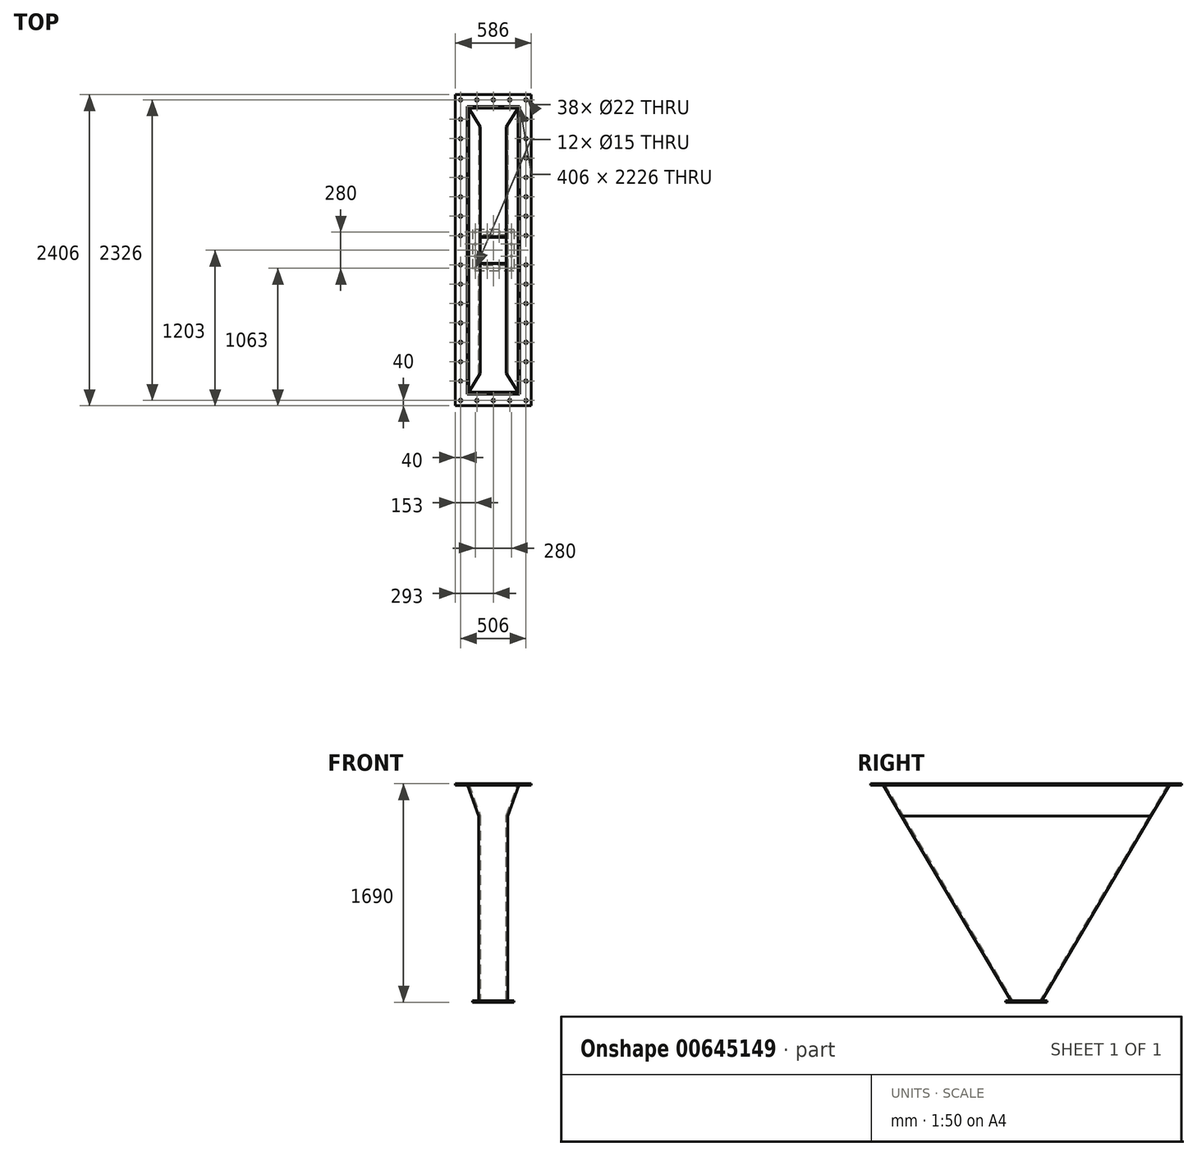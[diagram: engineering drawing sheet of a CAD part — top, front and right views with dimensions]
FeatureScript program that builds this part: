
annotation { "Feature Type Name" : "Feature", "Feature Type Description" : "" }
export const myFeature = defineFeature(function(context is Context, id is Id, definition is map)
    precondition{}
    {
        {
            var Q0;
            Q0=qCreatedBy(makeId("Front.planeOp"),FACE);
            var sketch = newSketch(context, id + "F0", { "sketchPlane" : qUnion([Q0])});
            skLineSegment(sketch, "E0", {"start": v(-203, 137.7) * mm, "end": v(203, 137.7) * mm});
            skLineSegment(sketch, "E1", {"start": v(0, 137.7) * mm, "end": v(0, -112.31) * mm, "construction": true});
            skLineSegment(sketch, "E2", {"start": v(-112, -112.31) * mm, "end": v(112, -112.31) * mm});
            skLineSegment(sketch, "E3", {"start": v(-203, 137.7) * mm, "end": v(-112, -112.31) * mm});
            skLineSegment(sketch, "E4", {"start": v(112, -112.31) * mm, "end": v(203, 137.7) * mm});
            skLineSegment(sketch, "E5", {"start": v(-112, -112.31) * mm, "end": v(-112, -1552.3) * mm});
            skLineSegment(sketch, "E6", {"start": v(-112, -1552.3) * mm, "end": v(112, -1552.3) * mm});
            skLineSegment(sketch, "E7", {"start": v(112, -1552.3) * mm, "end": v(112, -112.31) * mm});
            skLineSegment(sketch, "E8", {"start": v(-112, -112.31) * mm, "end": v(-112, 137.7) * mm, "construction": true});
            skLineSegment(sketch, "E9", {"start": v(112, -112.31) * mm, "end": v(112, 137.7) * mm, "construction": true});
            skSolve(sketch);
        }
        {
            var Q0;
            Q0=makeQuery(id+"F0.imprint","IMPRINT",FACE,{"disambiguationData":[TD([[makeQuery(id+"F0.imprint","IMPRINT",EDGE,{"derivedFrom":sQuery(id+"F0.wireOp",EDGE,"E0")}),-1.0]])]});
            var Q1;
            Q1=makeQuery(id+"F0.imprint","IMPRINT",FACE,{"disambiguationData":[TD([[makeQuery(id+"F0.imprint","IMPRINT",EDGE,{"derivedFrom":sQuery(id+"F0.wireOp",EDGE,"E2")}),-1.0]])]});
            extrude(context, id + "F1", {"entities" : qUnion([Q0, Q1]), "oppositeDirection" : true, "depth" : 2226 * mm, "offsetDistance" : 25 * mm});
        }
        {
            var Q0;
            Q0=makeQuery(id+"F1.opExtrude","SWEPT_FACE",FACE,{"disambiguationData":[OSD([sQuery(id+"F0.wireOp",EDGE,"E7")])]});
            var sketch = newSketch(context, id + "F2", { "sketchPlane" : qUnion([Q0])});
            skLineSegment(sketch, "E10", {"start": v(1113, -1552.3) * mm, "end": v(1113, -1167.4) * mm, "construction": true});
            skLineSegment(sketch, "E11", {"start": v(1113, -1552.3) * mm, "end": v(1225, -1552.3) * mm});
            skLineSegment(sketch, "E12", {"start": v(1225, -1552.3) * mm, "end": v(2226, 137.7) * mm});
            skLineSegment(sketch, "E13", {"start": v(2226, 137.7) * mm, "end": v(2226, -1552.3) * mm});
            skLineSegment(sketch, "E14", {"start": v(2226, -1552.3) * mm, "end": v(1225, -1552.3) * mm});
            skLineSegment(sketch, "E15.MirrorCS", {"start": v(1001, -1552.3) * mm, "end": v(0, 137.7) * mm});
            skLineSegment(sketch, "E16.MirrorCS", {"start": v(0, -1552.3) * mm, "end": v(1001, -1552.3) * mm});
            skLineSegment(sketch, "E17.MirrorCS", {"start": v(0, 137.7) * mm, "end": v(0, -1552.3) * mm});
            skSolve(sketch);
        }
        {
            var Q0;
            Q0 = qSketchRegion(id + "F2", true);
            extrude(context, id + "F3", {"entities" : qUnion([Q0]), "operationType" : NewBodyOperationType.REMOVE, "oppositeDirection" : true, "depth" : 400 * mm, "offsetDistance" : 25 * mm, "hasSecondDirection" : true, "secondDirectionOppositeDirection" : false, "secondDirectionDepth" : 400 * mm});
        }
        {
            var Q0;
            Q0=makeQuery(id+"F1.opExtrude","SWEPT_FACE",FACE,{"disambiguationData":[OSD([sQuery(id+"F0.wireOp",EDGE,"E0")])]});
            shell(context, id + "F4", {"entities" : qUnion([Q0]), "thickness" : 12 * mm});
        }
        {
            var Q0;
            Q0=makeQuery(id+"F1.opExtrude","SWEPT_FACE",FACE,{"disambiguationData":[OSD([sQuery(id+"F0.wireOp",EDGE,"E6")])]});
            var sketch = newSketch(context, id + "F5", { "sketchPlane" : qUnion([Q0])});
            skLineSegment(sketch, "E18.bottom", {"start": v(-100, -1013) * mm, "end": v(100, -1013) * mm});
            skLineSegment(sketch, "E18.top", {"start": v(-100, -1213) * mm, "end": v(100, -1213) * mm});
            skLineSegment(sketch, "E18.left", {"start": v(-100, -1013) * mm, "end": v(-100, -1213) * mm});
            skLineSegment(sketch, "E18.right", {"start": v(100, -1013) * mm, "end": v(100, -1213) * mm});
            skPoint(sketch, "E18.middle", {"position": v(0, -1113) * mm});
            skPoint(sketch, "E18.middle.positionSnap0", {"position": v(112, -1113) * mm});
            skPoint(sketch, "E18.middle.positionSnap1", {"position": v(0, -1225) * mm});
            skPoint(sketch, "E18.centerSnap0", {"position": v(112, -1113) * mm});
            skPoint(sketch, "E18.centerSnap1", {"position": v(0, -1225) * mm});
            skSolve(sketch);
        }
        {
            var Q0;
            Q0 = qSketchRegion(id + "F5", true);
            extrude(context, id + "F6", {"entities" : qUnion([Q0]), "operationType" : NewBodyOperationType.REMOVE, "endBound" : BoundingType.THROUGH_ALL, "oppositeDirection" : true, "depth" : 25 * mm, "offsetDistance" : 25 * mm});
        }
        {
            var Q0;
            Q0=makeQuery(id+"F1.opExtrude","SWEPT_FACE",FACE,{"disambiguationData":[OSD([sQuery(id+"F0.wireOp",EDGE,"E0")])]});
            var sketch = newSketch(context, id + "F7", { "sketchPlane" : qUnion([Q0])});
            skLineSegment(sketch, "E19.bottom", {"start": v(-203, 0) * mm, "end": v(203, 0) * mm});
            skLineSegment(sketch, "E19.top", {"start": v(-203, 2226) * mm, "end": v(203, 2226) * mm});
            skLineSegment(sketch, "E19.left", {"start": v(-203, 0) * mm, "end": v(-203, 2226) * mm});
            skLineSegment(sketch, "E19.right", {"start": v(203, 0) * mm, "end": v(203, 2226) * mm});
            skLineSegment(sketch, "E20.bottom", {"start": v(-293, 2316) * mm, "end": v(293, 2316) * mm});
            skLineSegment(sketch, "E20.top", {"start": v(-293, -90) * mm, "end": v(293, -90) * mm});
            skLineSegment(sketch, "E20.left", {"start": v(-293, 2316) * mm, "end": v(-293, -90) * mm});
            skLineSegment(sketch, "E20.right", {"start": v(293, 2316) * mm, "end": v(293, -90) * mm});
            skPoint(sketch, "E20.middle", {"position": v(0, 1113) * mm});
            skPoint(sketch, "E20.middle.positionSnap0", {"position": v(-203, 1113) * mm});
            skPoint(sketch, "E20.middle.positionSnap1", {"position": v(0, 13.95) * mm});
            skPoint(sketch, "E20.centerSnap0", {"position": v(-203, 1113) * mm});
            skPoint(sketch, "E20.centerSnap1", {"position": v(0, 13.95) * mm});
            skCircle(sketch, "E21", {"center": v(0, -50) * mm, "radius": 11 * mm});
            skCircle(sketch, "E22", {"center": v(127, -50) * mm, "radius": 11 * mm});
            skCircle(sketch, "E23", {"center": v(253, -50) * mm, "radius": 11 * mm});
            skCircle(sketch, "E24", {"center": v(253, 100) * mm, "radius": 11 * mm});
            skCircle(sketch, "E25", {"center": v(253, 1000) * mm, "radius": 11 * mm});
            skCircle(sketch, "E26", {"center": v(253, 850) * mm, "radius": 11 * mm});
            skCircle(sketch, "E27", {"center": v(253, 700) * mm, "radius": 11 * mm});
            skCircle(sketch, "E28", {"center": v(253, 550) * mm, "radius": 11 * mm});
            skCircle(sketch, "E29", {"center": v(253, 400) * mm, "radius": 11 * mm});
            skCircle(sketch, "E30", {"center": v(253, 250) * mm, "radius": 11 * mm});
            skLineSegment(sketch, "E31", {"start": v(0, 1113) * mm, "end": v(-353.58, 1113) * mm, "construction": true});
            skCircle(sketch, "E32.MirrorC", {"center": v(253, 1226) * mm, "radius": 11 * mm});
            skCircle(sketch, "E33.MirrorC", {"center": v(253, 1376) * mm, "radius": 11 * mm});
            skCircle(sketch, "E34.MirrorC", {"center": v(253, 1526) * mm, "radius": 11 * mm});
            skCircle(sketch, "E35.MirrorC", {"center": v(253, 1676) * mm, "radius": 11 * mm});
            skCircle(sketch, "E36.MirrorC", {"center": v(253, 1826) * mm, "radius": 11 * mm});
            skCircle(sketch, "E37.MirrorC", {"center": v(253, 1976) * mm, "radius": 11 * mm});
            skCircle(sketch, "E38.MirrorC", {"center": v(253, 2126) * mm, "radius": 11 * mm});
            skCircle(sketch, "E39.MirrorC", {"center": v(253, 2276) * mm, "radius": 11 * mm});
            skCircle(sketch, "E40.MirrorC", {"center": v(127, 2276) * mm, "radius": 11 * mm});
            skCircle(sketch, "E41.MirrorC", {"center": v(0, 2276) * mm, "radius": 11 * mm});
            skLineSegment(sketch, "E42", {"start": v(0, 1028.55) * mm, "end": v(0, 1182.62) * mm, "construction": true});
            skCircle(sketch, "E43.MirrorC", {"center": v(-127, 2276) * mm, "radius": 11 * mm});
            skCircle(sketch, "E44.MirrorC", {"center": v(-253, 2276) * mm, "radius": 11 * mm});
            skCircle(sketch, "E45.MirrorC", {"center": v(-253, 2126) * mm, "radius": 11 * mm});
            skCircle(sketch, "E46.MirrorC", {"center": v(-253, 1976) * mm, "radius": 11 * mm});
            skCircle(sketch, "E47.MirrorC", {"center": v(-253, 1826) * mm, "radius": 11 * mm});
            skCircle(sketch, "E48.MirrorC", {"center": v(-253, 1676) * mm, "radius": 11 * mm});
            skCircle(sketch, "E49.MirrorC", {"center": v(-253, 1526) * mm, "radius": 11 * mm});
            skCircle(sketch, "E50.MirrorC", {"center": v(-253, 1376) * mm, "radius": 11 * mm});
            skCircle(sketch, "E51.MirrorC", {"center": v(-253, 1226) * mm, "radius": 11 * mm});
            skCircle(sketch, "E52.MirrorC", {"center": v(-253, 1000) * mm, "radius": 11 * mm});
            skCircle(sketch, "E53.MirrorC", {"center": v(-253, 850) * mm, "radius": 11 * mm});
            skCircle(sketch, "E54.MirrorC", {"center": v(-253, 700) * mm, "radius": 11 * mm});
            skCircle(sketch, "E55.MirrorC", {"center": v(-253, 550) * mm, "radius": 11 * mm});
            skCircle(sketch, "E56.MirrorC", {"center": v(-253, 400) * mm, "radius": 11 * mm});
            skCircle(sketch, "E57.MirrorC", {"center": v(-253, 250) * mm, "radius": 11 * mm});
            skCircle(sketch, "E58.MirrorC", {"center": v(-253, 100) * mm, "radius": 11 * mm});
            skCircle(sketch, "E59.MirrorC", {"center": v(-253, -50) * mm, "radius": 11 * mm});
            skCircle(sketch, "E60.MirrorC", {"center": v(-127, -50) * mm, "radius": 11 * mm});
            skSolve(sketch);
        }
        {
            var Q0;
            Q0 = qSketchRegion(id + "F7", true);
            extrude(context, id + "F8", {"entities" : qUnion([Q0]), "oppositeDirection" : true, "depth" : 12 * mm, "offsetDistance" : 25 * mm});
        }
        {
            var Q0;
            Q0=makeQuery(id+"F1.opExtrude","SWEPT_FACE",FACE,{"disambiguationData":[OSD([sQuery(id+"F0.wireOp",EDGE,"E6")])]});
            var sketch = newSketch(context, id + "F9", { "sketchPlane" : qUnion([Q0])});
            skLineSegment(sketch, "E61", {"start": v(0, -943.32) * mm, "end": v(0, -1281.15) * mm, "construction": true});
            skPoint(sketch, "E61.startSnap0", {"position": v(0, -1001) * mm});
            skPoint(sketch, "E61.endSnap0", {"position": v(0, -1225) * mm});
            skLineSegment(sketch, "E62", {"start": v(143.58, -1113) * mm, "end": v(-139.48, -1113) * mm, "construction": true});
            skPoint(sketch, "E62.startSnap0", {"position": v(112, -1113) * mm});
            skLineSegment(sketch, "E63.bottom", {"start": v(160, -1273) * mm, "end": v(-160, -1273) * mm});
            skLineSegment(sketch, "E63.top", {"start": v(160, -953) * mm, "end": v(-160, -953) * mm});
            skLineSegment(sketch, "E63.left", {"start": v(160, -1273) * mm, "end": v(160, -953) * mm});
            skLineSegment(sketch, "E63.right", {"start": v(-160, -1273) * mm, "end": v(-160, -953) * mm});
            skPoint(sketch, "E63.middle", {"position": v(0, -1113) * mm});
            skLineSegment(sketch, "E64.bottom", {"start": v(112, -1225) * mm, "end": v(-112, -1225) * mm});
            skLineSegment(sketch, "E64.top", {"start": v(112, -1001) * mm, "end": v(-112, -1001) * mm});
            skLineSegment(sketch, "E64.left", {"start": v(112, -1225) * mm, "end": v(112, -1001) * mm});
            skLineSegment(sketch, "E64.right", {"start": v(-112, -1225) * mm, "end": v(-112, -1001) * mm});
            skSolve(sketch);
        }
        {
            var Q0;
            Q0 = qSketchRegion(id + "F9", true);
            extrude(context, id + "F10", {"entities" : qUnion([Q0]), "operationType" : NewBodyOperationType.ADD, "oppositeDirection" : true, "depth" : 12 * mm, "offsetDistance" : 25 * mm});
        }
        {
            var Q0;
            Q0=makeQuery(id+"F10.boolean.opBoolean","MERGE",FACE,{"derivedFrom":[makeQuery(id+"F1.opExtrude","SWEPT_FACE",FACE,{"disambiguationData":[OSD([sQuery(id+"F0.wireOp",EDGE,"E6")])]}),makeQuery(id+"F10.opExtrude","CAP_FACE",FACE,{"disambiguationData":[OSD([sQuery(id+"F9.wireOp",EDGE,"E63.bottom"),sQuery(id+"F9.wireOp",EDGE,"E63.top"),sQuery(id+"F9.wireOp",EDGE,"E63.left"),sQuery(id+"F9.wireOp",EDGE,"E63.right"),sQuery(id+"F9.wireOp",EDGE,"E64.bottom"),sQuery(id+"F9.wireOp",EDGE,"E64.top"),sQuery(id+"F9.wireOp",EDGE,"E64.left"),sQuery(id+"F9.wireOp",EDGE,"E64.right")])],"isStart":true})]});
            var sketch = newSketch(context, id + "F11", { "sketchPlane" : qUnion([Q0])});
            skCircle(sketch, "E65", {"center": v(140, -973) * mm, "radius": 7.5 * mm});
            skCircle(sketch, "E66", {"center": v(140, -1066.35) * mm, "radius": 7.5 * mm});
            skCircle(sketch, "E67", {"center": v(46.65, -973) * mm, "radius": 7.5 * mm});
            skLineSegment(sketch, "E68", {"start": v(183.93, -1113) * mm, "end": v(-193.93, -1113) * mm, "construction": true});
            skPoint(sketch, "E68.startSnap0", {"position": v(160, -1113) * mm});
            skLineSegment(sketch, "E69", {"start": v(0, -890.07) * mm, "end": v(0, -1356.24) * mm, "construction": true});
            skPoint(sketch, "E69.startSnap0", {"position": v(0, -1013) * mm});
            skPoint(sketch, "E69.endSnap0", {"position": v(0, -1273) * mm});
            skCircle(sketch, "E70.MirrorC", {"center": v(140, -1159.65) * mm, "radius": 7.5 * mm});
            skCircle(sketch, "E71.MirrorC", {"center": v(140, -1253) * mm, "radius": 7.5 * mm});
            skCircle(sketch, "E72.MirrorC", {"center": v(46.65, -1253) * mm, "radius": 7.5 * mm});
            skCircle(sketch, "E73.MirrorC", {"center": v(-46.65, -973) * mm, "radius": 7.5 * mm});
            skCircle(sketch, "E74.MirrorC", {"center": v(-140, -973) * mm, "radius": 7.5 * mm});
            skCircle(sketch, "E75.MirrorC", {"center": v(-140, -1066.35) * mm, "radius": 7.5 * mm});
            skCircle(sketch, "E76.MirrorC", {"center": v(-140, -1159.65) * mm, "radius": 7.5 * mm});
            skCircle(sketch, "E77.MirrorC", {"center": v(-140, -1253) * mm, "radius": 7.5 * mm});
            skCircle(sketch, "E78.MirrorC", {"center": v(-46.65, -1253) * mm, "radius": 7.5 * mm});
            skSolve(sketch);
        }
        {
            var Q0;
            Q0 = qSketchRegion(id + "F11", true);
            extrude(context, id + "F12", {"entities" : qUnion([Q0]), "operationType" : NewBodyOperationType.REMOVE, "oppositeDirection" : true, "depth" : 12 * mm, "offsetDistance" : 25 * mm});
        }
    });
